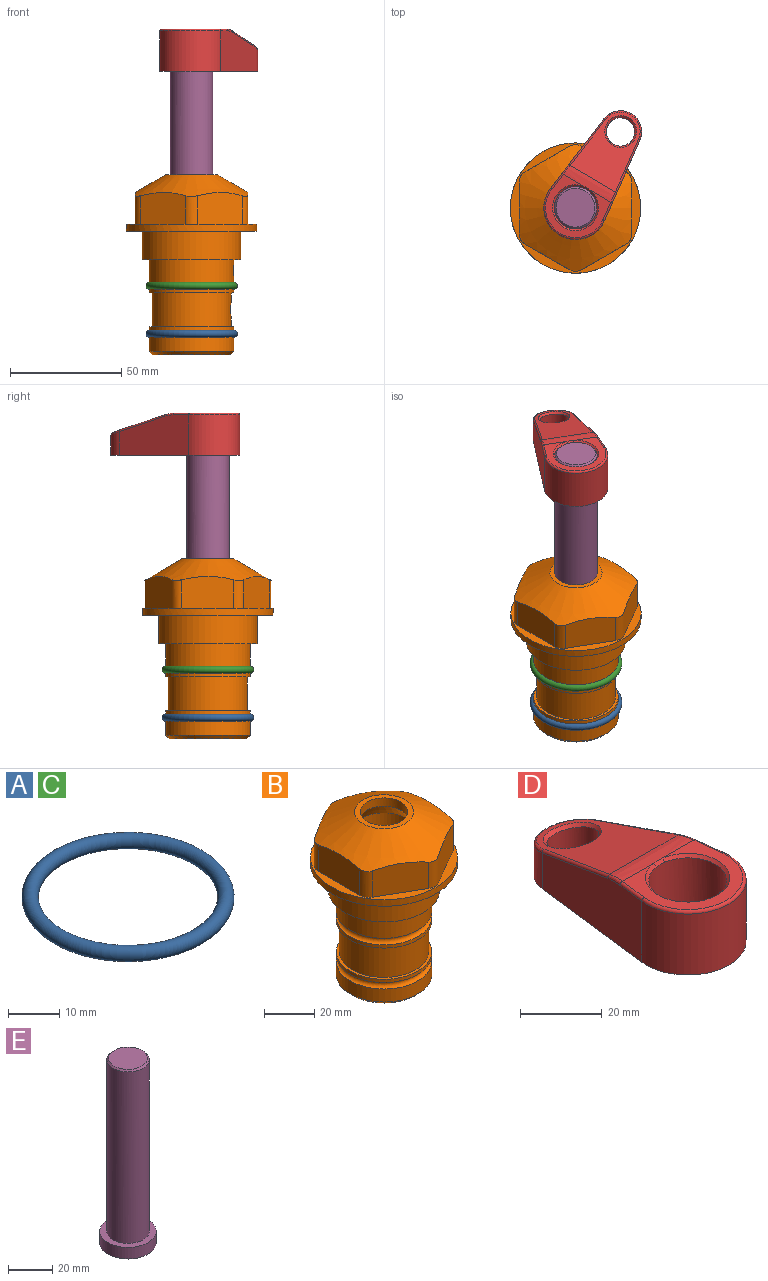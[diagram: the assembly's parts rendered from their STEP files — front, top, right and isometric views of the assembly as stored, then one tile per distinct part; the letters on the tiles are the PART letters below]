
ASSEMBLY  parts=5 mates=4
PART A: 1 faces, bbox 44.7x44.7x3.2 mm
  f0: torus R=19.05mm, axis (0,0,1), area 1193.9mm2
PART B: 36 faces, bbox 58.7x58.7x81 mm
  f0: cylinder r=17.78mm len=35.56mm, axis (0,0,1), area 1670.8mm2, adj f23,f24,f31
  f1: cylinder r=19.05mm len=38.1mm, axis (0,0,1), area 1191.9mm2, adj f26,f27,f30
  f2: plane 58.66x58.66mm, normal (0,0,-1), area 1150.6mm2, adj f3,f28
  f3: cylinder r=29.33mm len=58.66mm, axis (0,0,-1), area 585.1mm2, adj f2,f4
  f4: plane 58.66x58.66mm, normal (0,0,1), area 475.9mm2, adj f3,f5,f6,f7,f8,f9,f10,f11
  f5: plane 20.32x14.34mm, normal (-0.5,0.87,0), area 324.4mm2, adj f4,f15,f16,f17
  f6: plane 20.32x14.34mm, normal (0.5,0.87,0), area 324.4mm2, adj f4,f14,f15,f17
  f7: plane 23.48x14.34mm, normal (1,0,0), area 324.4mm2, adj f4,f13,f14,f17
  f8: plane 20.32x14.34mm, normal (0.5,-0.87,0), area 324.4mm2, adj f4,f12,f13,f17
  f9: plane 20.32x14.34mm, normal (-0.5,-0.87,0), area 324.4mm2, adj f4,f11,f12,f17
  f10: plane 23.48x14.34mm, normal (-1,0,0), area 324.4mm2, adj f4,f11,f16,f17
  f11: cylinder r=5.08mm len=12.85mm, axis (0,0,-1), area 67.2mm2, adj f4,f9,f10,f17
  f12: cylinder r=5.08mm len=12.85mm, axis (0,0,-1), area 67.2mm2, adj f4,f8,f9,f17
  f13: cylinder r=5.08mm len=12.85mm, axis (0,0,-1), area 67.2mm2, adj f4,f7,f8,f17
  f14: cylinder r=5.08mm len=12.85mm, axis (0,0,-1), area 67.2mm2, adj f4,f6,f7,f17
  f15: cylinder r=5.08mm len=12.85mm, axis (0,0,-1), area 67.2mm2, adj f4,f5,f6,f17
  f16: cylinder r=5.08mm len=12.85mm, axis (0,0,-1), area 67.2mm2, adj f4,f5,f10,f17
  f17: cone r=11.73mm half-angle=60deg, axis (0,0,-1), area 2071.8mm2, adj f5,f6,f7,f8,f9,f10,f11,f12
  f18: plane 23.46x23.46mm, normal (0,0,1), area 147.4mm2, adj f17,f35
  f19: plane 34.93x34.93mm, normal (0,0,-1), area 958mm2, adj f29
  f20: cylinder r=19.05mm len=38.1mm, axis (0,0,1), area 760.1mm2, adj f21,f29
  f21: torus R=19.05mm, axis (0,0,1), area 565.3mm2, adj f20,f22
  f22: cylinder r=19.05mm len=38.1mm, axis (0,0,1), area 190mm2, adj f21,f23
  f23: plane 38.1x38.1mm, normal (0,0,1), area 146.9mm2, adj f0,f22
  f24: plane 38.1x38.1mm, normal (0,0,-1), area 146.9mm2, adj f0,f25
  f25: cylinder r=19.05mm len=38.1mm, axis (0,0,1), area 190mm2, adj f24,f26
  f26: torus R=19.05mm, axis (0,0,1), area 565.3mm2, adj f1,f25
  f27: plane 44.45x44.45mm, normal (0,0,-1), area 411.7mm2, adj f1,f28
  f28: cylinder r=22.23mm len=44.45mm, axis (0,0,1), area 1773.5mm2, adj f2,f27
  f29: cone r=19.05mm half-angle=45deg, axis (0,0,1), area 257.5mm2, adj f19,f20
  f30: cylinder r=3.17mm len=6.75mm, axis (-1,0,0), area 128mm2, adj f1,f33
  f31: cylinder r=3.17mm len=6.35mm, axis (-1,0,0), area 102.5mm2, adj f0,f33
  f32: plane 25.4x25.4mm, normal (0,0,1), area 506.7mm2, adj f33
  f33: cylinder r=12.7mm len=66.42mm, axis (0,0,-1), area 5236.2mm2, adj f30,f31,f32,f34
  f34: cone r=9.53mm half-angle=30deg, axis (0,0,-1), area 443.4mm2, adj f33,f35
  f35: cylinder r=9.53mm len=19.05mm, axis (0,0,-1), area 240.9mm2, adj f18,f34
PART C: same geometry as A
PART D: 31 faces, bbox 31.7x65.5x19.8 mm
  f0: plane 39.12x18.26mm, normal (0.99,0.12,0), area 612.2mm2, adj f1,f4,f7,f11,f13,f15
  f1: cylinder r=9.53mm len=18.91mm, axis (0,0,-1), area 296.1mm2, adj f0,f2,f7,f17
  f2: plane 39.12x18.26mm, normal (-0.99,0.12,0), area 612.2mm2, adj f1,f4,f7,f12,f14,f16
  f3: cylinder r=6.35mm len=12.7mm, axis (0,0,-1), area 362.4mm2, adj f7,f18
  f4: cylinder r=14.29mm len=28.58mm, axis (0,0,-1), area 882.2mm2, adj f0,f2,f7,f10
  f5: cylinder r=9.53mm len=19.05mm, axis (0,0,-1), area 1092.6mm2, adj f7,f19,f20
  f6: plane 26.99x23.69mm, normal (0,0,1), area 216.2mm2, adj f9,f10,f11,f12,f19
  f7: plane 63.5x28.58mm, normal (0,0,-1), area 661.8mm2, adj f0,f1,f2,f3,f4,f5,f22,f23
  f8: plane 33.52x23.6mm, normal (0,0.26,0.97), area 486mm2, adj f9,f15,f16,f17,f18
  f9: cylinder r=19.05mm len=24.72mm, axis (1,0,0), area 120.4mm2, adj f6,f8,f13,f14,f20
  f10: torus R=13.49mm, axis (0,0,1), area 59mm2, adj f4,f6,f11,f12
  f11: cylinder r=0.79mm len=8.67mm, axis (0.12,-0.99,0), area 10.8mm2, adj f0,f6,f10,f13
  f12: cylinder r=0.79mm len=8.67mm, axis (0.12,0.99,0), area 10.8mm2, adj f2,f6,f10,f14
  f13: bspline ~4.95x1.42mm, area 6.1mm2, adj f0,f9,f11,f15
  f14: bspline ~4.95x1.42mm, area 6.1mm2, adj f2,f9,f12,f16
  f15: cylinder r=0.79mm len=25.95mm, axis (0.12,-0.96,0.26), area 32.9mm2, adj f0,f8,f13,f17
  f16: cylinder r=0.79mm len=25.95mm, axis (0.12,0.96,-0.26), area 32.9mm2, adj f2,f8,f14,f17
  f17: bspline ~18.91x8.38mm, area 30mm2, adj f1,f8,f15,f16
  f18: bspline ~14.29x14.29mm, area 48.3mm2, adj f3,f8
  f19: cone r=9.53mm half-angle=45deg, axis (0,0,1), area 66.5mm2, adj f5,f6,f20
  f20: bspline ~3.22x0.96mm, area 3.5mm2, adj f5,f9,f19
  f21: plane 2.75x2.72mm, normal (0,0,-1), area 2.9mm2, adj f23,f25,f28
  f22: plane 23.05x15.88mm, normal (-0.99,-0.12,0), area 323.6mm2, adj f7,f25,f26,f27,f28,f29
  f23: plane 23.05x15.88mm, normal (0.99,-0.12,0), area 323.6mm2, adj f7,f21,f25,f27,f28,f30
  f24: cylinder r=9.53mm len=10.69mm, axis (0,0,-1), area 114.7mm2, adj f7,f27,f29,f30
  f25: cylinder r=12.7mm len=20.59mm, axis (0,0,-1), area 381.1mm2, adj f7,f21,f22,f23,f26,f28
  f26: plane 2.75x2.72mm, normal (0,0,-1), area 2.9mm2, adj f22,f25,f28
  f27: plane 19.72x18.37mm, normal (0,-0.26,-0.97), area 291.8mm2, adj f22,f23,f24,f28,f29,f30
  f28: cylinder r=15.88mm len=19.92mm, axis (1,0,0), area 54.8mm2, adj f21,f22,f23,f25,f26,f27
  f29: cylinder r=1.59mm len=11mm, axis (0,0,-1), area 34.7mm2, adj f7,f22,f24,f27
  f30: cylinder r=1.59mm len=11mm, axis (0,0,-1), area 34.7mm2, adj f7,f23,f24,f27
PART E: 6 faces, bbox 25.4x25.4x101.6 mm
  f0: plane 17.46x17.46mm, normal (0,0,1), area 239.5mm2, adj f5
  f1: plane 25.4x25.4mm, normal (0,0,-1), area 506.7mm2, adj f2
  f2: cylinder r=12.7mm len=25.4mm, axis (0,0,1), area 506.7mm2, adj f1,f3
  f3: plane 25.4x25.4mm, normal (0,0,1), area 221.7mm2, adj f2,f4
  f4: cylinder r=9.53mm len=94.46mm, axis (0,0,1), area 5653mm2, adj f3,f5
  f5: cone r=8.73mm half-angle=45deg, axis (0,0,-1), area 64.4mm2, adj f0,f4
PLACE A t=(0,0,-21.59)mm
PLACE B at identity fixed
PLACE C at identity
PLACE D rot(axis=(0,0,-1),30.7deg) t=(0,0,27.55)mm
PLACE E rot(axis=(0,0,-1),30.7deg) t=(0,0,27.55)mm
MATE fastened E.f2 <-> D.f4  axis (0,0,1) through (0,0,91.05)mm
MATE cylindrical E.f2 <-> B.f0  axis (0,0,-1) through (0,0,-10.55)mm
MATE fastened A.f0 <-> B.f0  axis (0,0,1) through (0,0,-46.1)mm
MATE fastened C.f0 <-> B.f0  axis (0,0,1) through (0,0,-24.51)mm
